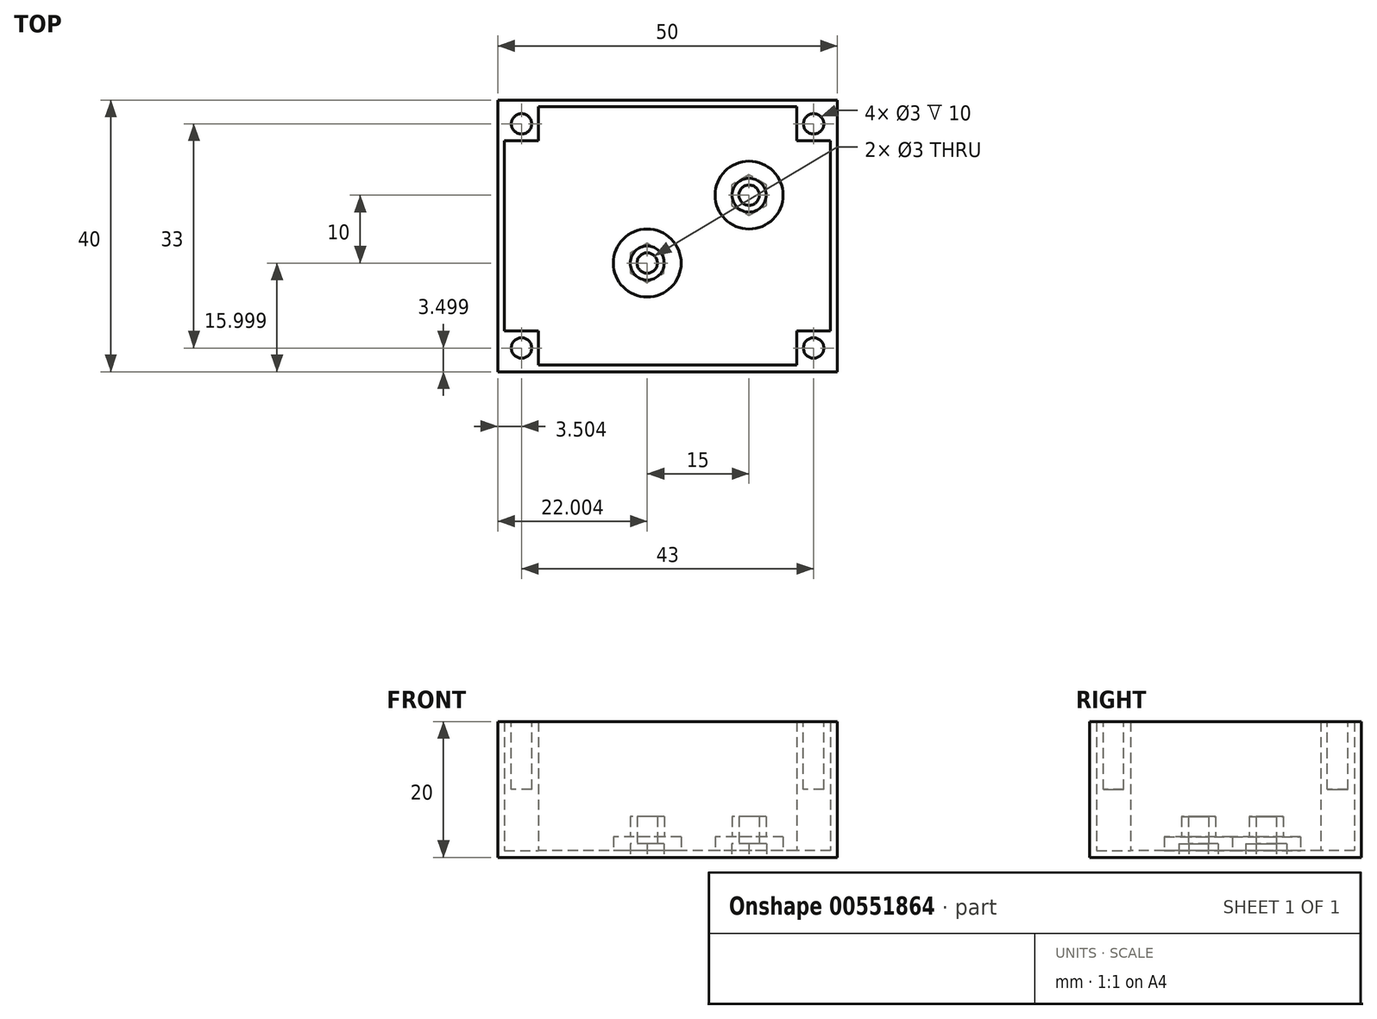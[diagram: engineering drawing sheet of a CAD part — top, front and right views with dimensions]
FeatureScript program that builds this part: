
annotation { "Feature Type Name" : "Feature", "Feature Type Description" : "" }
export const myFeature = defineFeature(function(context is Context, id is Id, definition is map)
    precondition{}
    {
        {
            var Q0;
            Q0=qCreatedBy(makeId("Top.planeOp"),FACE);
            var sketch = newSketch(context, id + "F0", { "sketchPlane" : qUnion([Q0])});
            skLineSegment(sketch, "E0.bottom", {"start": v(-55.78, 44.59) * mm, "end": v(-5.78, 44.59) * mm});
            skLineSegment(sketch, "E0.top", {"start": v(-55.78, 4.59) * mm, "end": v(-5.78, 4.59) * mm});
            skLineSegment(sketch, "E0.left", {"start": v(-55.78, 44.59) * mm, "end": v(-55.78, 4.59) * mm});
            skLineSegment(sketch, "E0.right", {"start": v(-5.78, 44.59) * mm, "end": v(-5.78, 4.59) * mm});
            skSolve(sketch);
        }
        {
            var Q0;
            Q0=makeQuery(id+"F0.imprint","IMPRINT",FACE,{"disambiguationData":[TD([[makeQuery(id+"F0.imprint","IMPRINT",EDGE,{"derivedFrom":sQuery(id+"F0.wireOp",EDGE,"E0.bottom")}),-1.0]])]});
            extrude(context, id + "F1", {"entities" : qUnion([Q0]), "depth" : 20 * mm, "offsetDistance" : 25 * mm});
        }
        {
            var Q0;
            Q0=makeQuery(id+"F1.opExtrude","CAP_FACE",FACE,{"disambiguationData":[OSD([sQuery(id+"F0.wireOp",EDGE,"E0.bottom"),sQuery(id+"F0.wireOp",EDGE,"E0.top"),sQuery(id+"F0.wireOp",EDGE,"E0.left"),sQuery(id+"F0.wireOp",EDGE,"E0.right")])],"isStart":false});
            var sketch = newSketch(context, id + "F2", { "sketchPlane" : qUnion([Q0])});
            skLineSegment(sketch, "E1.bottom", {"start": v(-6.78, 43.59) * mm, "end": v(-54.78, 43.59) * mm});
            skLineSegment(sketch, "E1.top", {"start": v(-6.78, 5.59) * mm, "end": v(-54.78, 5.59) * mm});
            skLineSegment(sketch, "E1.left", {"start": v(-6.78, 43.59) * mm, "end": v(-6.78, 5.59) * mm});
            skLineSegment(sketch, "E1.right", {"start": v(-54.78, 43.59) * mm, "end": v(-54.78, 5.59) * mm});
            skPoint(sketch, "E1.middle", {"position": v(-30.78, 24.59) * mm});
            skPoint(sketch, "E1.middle.positionSnap0", {"position": v(-5.78, 24.59) * mm});
            skPoint(sketch, "E1.middle.positionSnap1", {"position": v(-30.78, 44.59) * mm});
            skPoint(sketch, "E1.centerSnap0", {"position": v(-5.78, 24.59) * mm});
            skPoint(sketch, "E1.centerSnap1", {"position": v(-30.78, 44.59) * mm});
            skSolve(sketch);
        }
        {
            var Q0;
            Q0=makeQuery(id+"F2.imprint","IMPRINT",FACE,{"disambiguationData":[TD([[makeQuery(id+"F2.imprint","IMPRINT",EDGE,{"derivedFrom":sQuery(id+"F2.wireOp",EDGE,"E1.bottom")}),1.0]])]});
            extrude(context, id + "F3", {"entities" : qUnion([Q0]), "operationType" : NewBodyOperationType.REMOVE, "oppositeDirection" : true, "depth" : 19 * mm, "offsetDistance" : 25 * mm});
        }
        {
            var Q0;
            Q0=makeQuery(id+"F3.boolean.opBoolean","COPY",FACE,{"derivedFrom":makeQuery(id+"F3.opExtrude","CAP_FACE",FACE,{"disambiguationData":[OSD([sQuery(id+"F2.wireOp",EDGE,"E1.bottom"),sQuery(id+"F2.wireOp",EDGE,"E1.top"),sQuery(id+"F2.wireOp",EDGE,"E1.left"),sQuery(id+"F2.wireOp",EDGE,"E1.right")])],"isStart":false})});
            var sketch = newSketch(context, id + "F4", { "sketchPlane" : qUnion([Q0])});
            skLineSegment(sketch, "E2.bottom", {"start": v(-54.78, 43.59) * mm, "end": v(-49.78, 43.59) * mm});
            skLineSegment(sketch, "E2.top", {"start": v(-54.78, 38.59) * mm, "end": v(-49.78, 38.59) * mm});
            skLineSegment(sketch, "E2.left", {"start": v(-54.78, 43.59) * mm, "end": v(-54.78, 38.59) * mm});
            skLineSegment(sketch, "E2.right", {"start": v(-49.78, 43.59) * mm, "end": v(-49.78, 38.59) * mm});
            skLineSegment(sketch, "E3.bottom", {"start": v(-6.78, 5.59) * mm, "end": v(-11.78, 5.59) * mm});
            skLineSegment(sketch, "E3.top", {"start": v(-6.78, 10.59) * mm, "end": v(-11.78, 10.59) * mm});
            skLineSegment(sketch, "E3.left", {"start": v(-6.78, 5.59) * mm, "end": v(-6.78, 10.59) * mm});
            skLineSegment(sketch, "E3.right", {"start": v(-11.78, 5.59) * mm, "end": v(-11.78, 10.59) * mm});
            skLineSegment(sketch, "E4.bottom", {"start": v(-54.78, 5.59) * mm, "end": v(-49.78, 5.59) * mm});
            skLineSegment(sketch, "E4.top", {"start": v(-54.78, 10.59) * mm, "end": v(-49.78, 10.59) * mm});
            skLineSegment(sketch, "E4.left", {"start": v(-54.78, 5.59) * mm, "end": v(-54.78, 10.59) * mm});
            skLineSegment(sketch, "E4.right", {"start": v(-49.78, 5.59) * mm, "end": v(-49.78, 10.59) * mm});
            skLineSegment(sketch, "E5.bottom", {"start": v(-6.78, 43.59) * mm, "end": v(-11.78, 43.59) * mm});
            skLineSegment(sketch, "E5.top", {"start": v(-6.78, 38.59) * mm, "end": v(-11.78, 38.59) * mm});
            skLineSegment(sketch, "E5.left", {"start": v(-6.78, 43.59) * mm, "end": v(-6.78, 38.59) * mm});
            skLineSegment(sketch, "E5.right", {"start": v(-11.78, 43.59) * mm, "end": v(-11.78, 38.59) * mm});
            skSolve(sketch);
        }
        {
            var Q0;
            Q0=makeQuery(id+"F4.imprint","IMPRINT",FACE,{"disambiguationData":[TD([[makeQuery(id+"F4.imprint","IMPRINT",EDGE,{"derivedFrom":sQuery(id+"F4.wireOp",EDGE,"E2.bottom")}),1.0]])]});
            var Q1;
            Q1=makeQuery(id+"F4.imprint","IMPRINT",FACE,{"disambiguationData":[TD([[makeQuery(id+"F4.imprint","IMPRINT",EDGE,{"derivedFrom":sQuery(id+"F4.wireOp",EDGE,"E5.bottom")}),1.0]])]});
            var Q2;
            Q2=makeQuery(id+"F4.imprint","IMPRINT",FACE,{"disambiguationData":[TD([[makeQuery(id+"F4.imprint","IMPRINT",EDGE,{"derivedFrom":sQuery(id+"F4.wireOp",EDGE,"E3.bottom")}),-1.0]])]});
            var Q3;
            Q3=makeQuery(id+"F4.imprint","IMPRINT",FACE,{"disambiguationData":[TD([[makeQuery(id+"F4.imprint","IMPRINT",EDGE,{"derivedFrom":sQuery(id+"F4.wireOp",EDGE,"E4.bottom")}),-1.0]])]});
            extrude(context, id + "F5", {"entities" : qUnion([Q0, Q1, Q2, Q3]), "operationType" : NewBodyOperationType.ADD, "depth" : 19 * mm, "offsetDistance" : 25 * mm});
        }
        {
            var Q0;
            Q0=makeQuery(id+"F5.boolean.opBoolean","MERGE",FACE,{"derivedFrom":[makeQuery(id+"F1.opExtrude","CAP_FACE",FACE,{"disambiguationData":[OSD([sQuery(id+"F0.wireOp",EDGE,"E0.bottom"),sQuery(id+"F0.wireOp",EDGE,"E0.top"),sQuery(id+"F0.wireOp",EDGE,"E0.left"),sQuery(id+"F0.wireOp",EDGE,"E0.right")])],"isStart":false}),makeQuery(id+"F5.opExtrude","CAP_FACE",FACE,{"disambiguationData":[OSD([sQuery(id+"F4.wireOp",EDGE,"E2.bottom"),sQuery(id+"F4.wireOp",EDGE,"E2.top"),sQuery(id+"F4.wireOp",EDGE,"E2.left"),sQuery(id+"F4.wireOp",EDGE,"E2.right")])],"isStart":false}),makeQuery(id+"F5.opExtrude","CAP_FACE",FACE,{"disambiguationData":[OSD([sQuery(id+"F4.wireOp",EDGE,"E3.bottom"),sQuery(id+"F4.wireOp",EDGE,"E3.top"),sQuery(id+"F4.wireOp",EDGE,"E3.left"),sQuery(id+"F4.wireOp",EDGE,"E3.right")])],"isStart":false}),makeQuery(id+"F5.opExtrude","CAP_FACE",FACE,{"disambiguationData":[OSD([sQuery(id+"F4.wireOp",EDGE,"E4.bottom"),sQuery(id+"F4.wireOp",EDGE,"E4.top"),sQuery(id+"F4.wireOp",EDGE,"E4.left"),sQuery(id+"F4.wireOp",EDGE,"E4.right")])],"isStart":false}),makeQuery(id+"F5.opExtrude","CAP_FACE",FACE,{"disambiguationData":[OSD([sQuery(id+"F4.wireOp",EDGE,"E5.bottom"),sQuery(id+"F4.wireOp",EDGE,"E5.top"),sQuery(id+"F4.wireOp",EDGE,"E5.left"),sQuery(id+"F4.wireOp",EDGE,"E5.right")])],"isStart":false})]});
            var sketch = newSketch(context, id + "F6", { "sketchPlane" : qUnion([Q0])});
            skCircle(sketch, "E6", {"center": v(-52.28, 8.09) * mm, "radius": 1.5 * mm});
            skPoint(sketch, "E6.centerSnap0", {"position": v(-49.78, 8.09) * mm});
            skPoint(sketch, "E6.centerSnap1", {"position": v(-52.28, 10.59) * mm});
            skCircle(sketch, "E7", {"center": v(-52.28, 41.09) * mm, "radius": 1.5 * mm});
            skPoint(sketch, "E7.centerSnap0", {"position": v(-49.78, 41.09) * mm});
            skPoint(sketch, "E7.centerSnap1", {"position": v(-52.28, 38.59) * mm});
            skCircle(sketch, "E8", {"center": v(-9.28, 41.09) * mm, "radius": 1.5 * mm});
            skPoint(sketch, "E8.centerSnap0", {"position": v(-11.78, 41.09) * mm});
            skPoint(sketch, "E8.centerSnap1", {"position": v(-9.28, 38.59) * mm});
            skCircle(sketch, "E9", {"center": v(-9.28, 8.09) * mm, "radius": 1.5 * mm});
            skPoint(sketch, "E9.centerSnap0", {"position": v(-11.78, 8.09) * mm});
            skPoint(sketch, "E9.centerSnap1", {"position": v(-9.28, 10.59) * mm});
            skSolve(sketch);
        }
        {
            var Q0;
            Q0=makeQuery(id+"F6.imprint","IMPRINT",FACE,{"disambiguationData":[TD([[makeQuery(id+"F6.imprint","IMPRINT",EDGE,{"derivedFrom":sQuery(id+"F6.wireOp",EDGE,"E6")}),1.0]])]});
            var Q1;
            Q1=makeQuery(id+"F6.imprint","IMPRINT",FACE,{"disambiguationData":[TD([[makeQuery(id+"F6.imprint","IMPRINT",EDGE,{"derivedFrom":sQuery(id+"F6.wireOp",EDGE,"E7")}),1.0]])]});
            var Q2;
            Q2=makeQuery(id+"F6.imprint","IMPRINT",FACE,{"disambiguationData":[TD([[makeQuery(id+"F6.imprint","IMPRINT",EDGE,{"derivedFrom":sQuery(id+"F6.wireOp",EDGE,"E8")}),1.0]])]});
            var Q3;
            Q3=makeQuery(id+"F6.imprint","IMPRINT",FACE,{"disambiguationData":[TD([[makeQuery(id+"F6.imprint","IMPRINT",EDGE,{"derivedFrom":sQuery(id+"F6.wireOp",EDGE,"E9")}),1.0]])]});
            extrude(context, id + "F7", {"entities" : qUnion([Q0, Q1, Q2, Q3]), "operationType" : NewBodyOperationType.REMOVE, "oppositeDirection" : true, "depth" : 10 * mm, "offsetDistance" : 25 * mm});
        }
        {
            var Q0;
            Q0=makeQuery(id+"F3.boolean.opBoolean","COPY",FACE,{"derivedFrom":makeQuery(id+"F3.opExtrude","CAP_FACE",FACE,{"disambiguationData":[OSD([sQuery(id+"F2.wireOp",EDGE,"E1.bottom"),sQuery(id+"F2.wireOp",EDGE,"E1.top"),sQuery(id+"F2.wireOp",EDGE,"E1.left"),sQuery(id+"F2.wireOp",EDGE,"E1.right")])],"isStart":false})});
            var sketch = newSketch(context, id + "F8", { "sketchPlane" : qUnion([Q0])});
            skCircle(sketch, "E10", {"center": v(-33.78, 20.59) * mm, "radius": 2.5 * mm});
            skCircle(sketch, "E11", {"center": v(-18.78, 30.59) * mm, "radius": 2.5 * mm});
            skCircle(sketch, "E12", {"center": v(-33.78, 20.59) * mm, "radius": 1.5 * mm});
            skCircle(sketch, "E13", {"center": v(-18.78, 30.59) * mm, "radius": 1.5 * mm});
            skSolve(sketch);
        }
        {
            var Q0;
            Q0=makeQuery(id+"F8.imprint","IMPRINT",FACE,{"disambiguationData":[TD([[makeQuery(id+"F8.imprint","IMPRINT",EDGE,{"derivedFrom":sQuery(id+"F8.wireOp",EDGE,"E10")}),1.0]])]});
            var Q1;
            Q1=makeQuery(id+"F8.imprint","IMPRINT",FACE,{"disambiguationData":[TD([[makeQuery(id+"F8.imprint","IMPRINT",EDGE,{"derivedFrom":sQuery(id+"F8.wireOp",EDGE,"E11")}),1.0]])]});
            extrude(context, id + "F9", {"entities" : qUnion([Q0, Q1]), "operationType" : NewBodyOperationType.ADD, "depth" : 5 * mm, "offsetDistance" : 25 * mm});
        }
        {
            var Q0;
            Q0=makeQuery(id+"F9.boolean.opBoolean","SPLIT",FACE,{"disambiguationData":[TD([makeQuery(id+"F9.opExtrude","SWEPT_FACE",FACE,{"disambiguationData":[OSD([sQuery(id+"F8.wireOp",EDGE,"E12")])]})])],"derivedFrom":makeQuery(id+"F3.boolean.opBoolean","COPY",FACE,{"derivedFrom":makeQuery(id+"F3.opExtrude","CAP_FACE",FACE,{"disambiguationData":[OSD([sQuery(id+"F2.wireOp",EDGE,"E1.bottom"),sQuery(id+"F2.wireOp",EDGE,"E1.top"),sQuery(id+"F2.wireOp",EDGE,"E1.left"),sQuery(id+"F2.wireOp",EDGE,"E1.right")])],"isStart":false})})});
            var Q1;
            Q1=makeQuery(id+"F9.boolean.opBoolean","SPLIT",FACE,{"disambiguationData":[TD([makeQuery(id+"F9.opExtrude","SWEPT_FACE",FACE,{"disambiguationData":[OSD([sQuery(id+"F8.wireOp",EDGE,"E13")])]})])],"derivedFrom":makeQuery(id+"F3.boolean.opBoolean","COPY",FACE,{"derivedFrom":makeQuery(id+"F3.opExtrude","CAP_FACE",FACE,{"disambiguationData":[OSD([sQuery(id+"F2.wireOp",EDGE,"E1.bottom"),sQuery(id+"F2.wireOp",EDGE,"E1.top"),sQuery(id+"F2.wireOp",EDGE,"E1.left"),sQuery(id+"F2.wireOp",EDGE,"E1.right")])],"isStart":false})})});
            extrude(context, id + "F10", {"entities" : qUnion([Q0, Q1]), "operationType" : NewBodyOperationType.REMOVE, "oppositeDirection" : true, "depth" : 2 * mm, "offsetDistance" : 25 * mm});
        }
        {
            var Q0;
            {var subQ0=sQuery(id+"F2.wireOp",EDGE,"E1.bottom");var subQ1=sQuery(id+"F2.wireOp",EDGE,"E1.top");var subQ2=sQuery(id+"F2.wireOp",EDGE,"E1.left");var subQ3=sQuery(id+"F2.wireOp",EDGE,"E1.right");Q0=makeQuery(id+"F9.boolean.opBoolean","SPLIT",FACE,{"disambiguationData":[TD([makeQuery(id+"F3.boolean.opBoolean","COPY",FACE,{"derivedFrom":makeQuery(id+"F3.opExtrude","SWEPT_FACE",FACE,{"disambiguationData":[OSD([subQ0])]})})])],"derivedFrom":makeQuery(id+"F3.boolean.opBoolean","COPY",FACE,{"derivedFrom":makeQuery(id+"F3.opExtrude","CAP_FACE",FACE,{"disambiguationData":[OSD([subQ0,subQ1,subQ2,subQ3])],"isStart":false})})});}
            var sketch = newSketch(context, id + "F11", { "sketchPlane" : qUnion([Q0])});
            skCircle(sketch, "E14", {"center": v(-33.78, 20.59) * mm, "radius": 5 * mm});
            skCircle(sketch, "E15", {"center": v(-18.78, 30.59) * mm, "radius": 5 * mm});
            skSolve(sketch);
        }
        {
            var Q0;
            Q0=makeQuery(id+"F11.imprint","IMPRINT",FACE,{"disambiguationData":[TD([[makeQuery(id+"F11.imprint","IMPRINT",EDGE,{"derivedFrom":sQuery(id+"F11.wireOp",EDGE,"E15")}),1.0]])]});
            var Q1;
            Q1=makeQuery(id+"F11.imprint","IMPRINT",FACE,{"disambiguationData":[TD([[makeQuery(id+"F11.imprint","IMPRINT",EDGE,{"derivedFrom":sQuery(id+"F11.wireOp",EDGE,"E14")}),1.0]])]});
            extrude(context, id + "F12", {"entities" : qUnion([Q0, Q1]), "operationType" : NewBodyOperationType.ADD, "depth" : 2 * mm, "offsetDistance" : 25 * mm});
        }
        {
            var Q0;
            Q0=makeQuery(id+"F1.opExtrude","CAP_FACE",FACE,{"disambiguationData":[OSD([sQuery(id+"F0.wireOp",EDGE,"E0.bottom"),sQuery(id+"F0.wireOp",EDGE,"E0.top"),sQuery(id+"F0.wireOp",EDGE,"E0.left"),sQuery(id+"F0.wireOp",EDGE,"E0.right")])],"isStart":true});
            var sketch = newSketch(context, id + "F13", { "sketchPlane" : qUnion([Q0])});
            skCircle(sketch, "E16", {"center": v(-18.78, -30.59) * mm, "radius": 3 * mm});
            skCircle(sketch, "E17", {"center": v(-33.78, -20.59) * mm, "radius": 2.88 * mm});
            skCircle(sketch, "E18.cCircle", {"center": v(-18.78, -30.59) * mm, "radius": 3 * mm, "construction": true});
            skLineSegment(sketch, "E18.0", {"start": v(-18.78, -33.59) * mm, "end": v(-21.37, -32.09) * mm});
            skLineSegment(sketch, "E18.1", {"start": v(-21.37, -32.09) * mm, "end": v(-21.37, -29.09) * mm});
            skLineSegment(sketch, "E18.2", {"start": v(-21.37, -29.09) * mm, "end": v(-18.78, -27.59) * mm});
            skLineSegment(sketch, "E18.3", {"start": v(-18.78, -27.59) * mm, "end": v(-16.18, -29.09) * mm});
            skLineSegment(sketch, "E18.4", {"start": v(-16.18, -29.09) * mm, "end": v(-16.18, -32.09) * mm});
            skLineSegment(sketch, "E18.5", {"start": v(-16.18, -32.09) * mm, "end": v(-18.78, -33.59) * mm});
            skCircle(sketch, "E19.cCircle", {"center": v(-33.78, -20.59) * mm, "radius": 2.88 * mm, "construction": true});
            skLineSegment(sketch, "E19.0", {"start": v(-33.78, -23.46) * mm, "end": v(-36.27, -22.03) * mm});
            skLineSegment(sketch, "E19.1", {"start": v(-36.27, -22.03) * mm, "end": v(-36.27, -19.15) * mm});
            skLineSegment(sketch, "E19.2", {"start": v(-36.27, -19.15) * mm, "end": v(-33.78, -17.71) * mm});
            skLineSegment(sketch, "E19.3", {"start": v(-33.78, -17.71) * mm, "end": v(-31.29, -19.15) * mm});
            skLineSegment(sketch, "E19.4", {"start": v(-31.29, -19.15) * mm, "end": v(-31.29, -22.03) * mm});
            skLineSegment(sketch, "E19.5", {"start": v(-31.29, -22.03) * mm, "end": v(-33.78, -23.46) * mm});
            skSolve(sketch);
        }
        {
            var Q0;
            Q0=makeQuery(id+"F13.imprint","IMPRINT",FACE,{"disambiguationData":[TD([[makeQuery(id+"F13.imprint","IMPRINT",EDGE,{"derivedFrom":sQuery(id+"F13.wireOp",EDGE,"E18.0")}),-1.0]])]});
            var Q1;
            Q1=makeQuery(id+"F13.imprint","IMPRINT",FACE,{"disambiguationData":[TD([[makeQuery(id+"F13.imprint","IMPRINT",EDGE,{"derivedFrom":sQuery(id+"F13.wireOp",EDGE,"E19.0")}),-1.0]])]});
            extrude(context, id + "F14", {"entities" : qUnion([Q0, Q1]), "operationType" : NewBodyOperationType.REMOVE, "oppositeDirection" : true, "depth" : 2 * mm, "offsetDistance" : 25 * mm});
        }
    });
